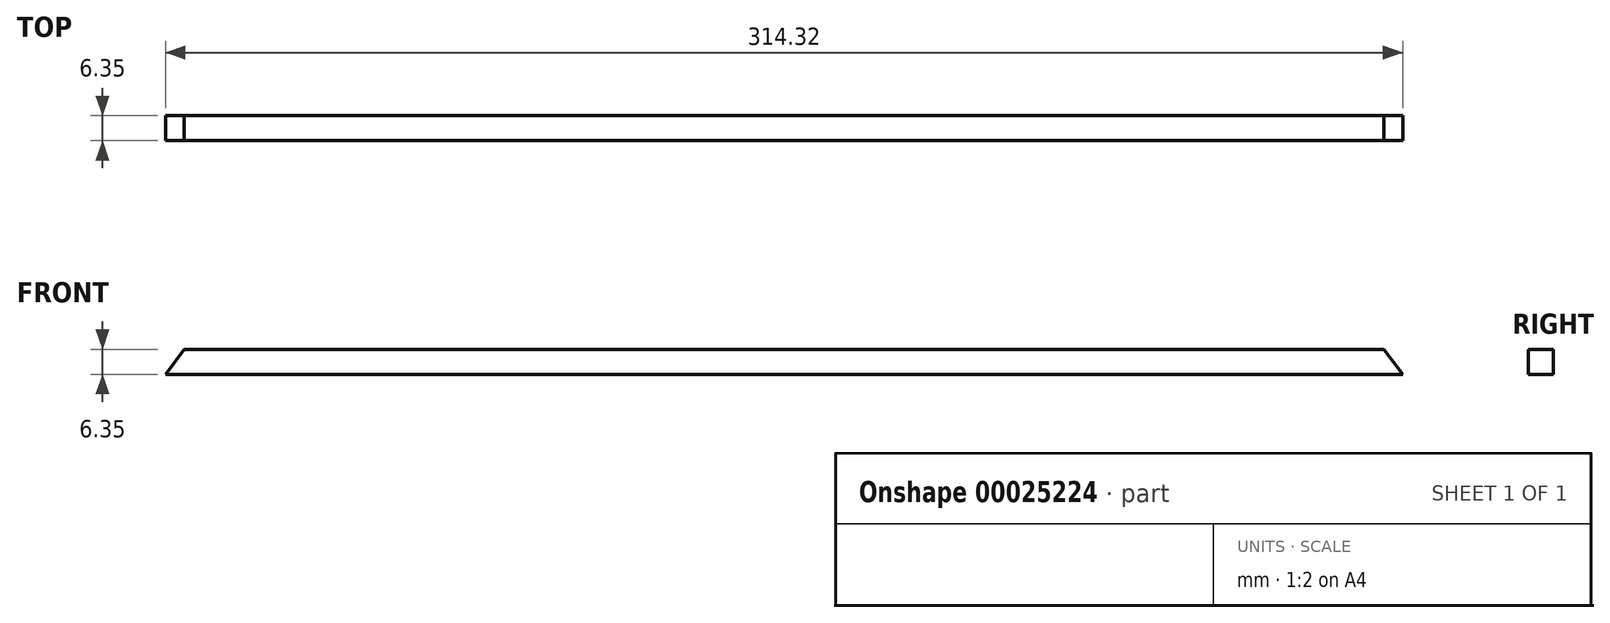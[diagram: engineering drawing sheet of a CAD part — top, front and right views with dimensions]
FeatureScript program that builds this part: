
annotation { "Feature Type Name" : "Feature", "Feature Type Description" : "" }
export const myFeature = defineFeature(function(context is Context, id is Id, definition is map)
    precondition{}
    {
        {
            var Q0;
            Q0=qCreatedBy(makeId("Front.planeOp"),FACE);
            var sketch = newSketch(context, id + "F0", { "sketchPlane" : qUnion([Q0])});
            skLineSegment(sketch, "E0", {"start": v(0, 0) * mm, "end": v(-4.76, 6.35) * mm});
            skLineSegment(sketch, "E1", {"start": v(-157.16, 6.35) * mm, "end": v(-4.76, 6.35) * mm});
            skLineSegment(sketch, "E2", {"start": v(0, 0) * mm, "end": v(-157.16, 0) * mm});
            skLineSegment(sketch, "E3", {"start": v(-157.16, 0) * mm, "end": v(-157.16, 6.35) * mm});
            skLineSegment(sketch, "E4.MirrorCS", {"start": v(-157.16, 6.35) * mm, "end": v(-309.56, 6.35) * mm});
            skLineSegment(sketch, "E5.MirrorCS", {"start": v(-314.32, 0) * mm, "end": v(-157.16, 0) * mm});
            skLineSegment(sketch, "E6.MirrorCS", {"start": v(-314.32, 0) * mm, "end": v(-309.56, 6.35) * mm});
            skSolve(sketch);
        }
        {
            var Q0;
            Q0=qSketchRegion(id+"F0",true);
            extrude(context, id + "F1", {"entities" : qUnion([Q0]), "depth" : 6.35 * mm});
        }
    });
